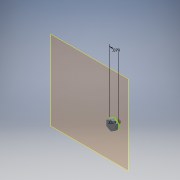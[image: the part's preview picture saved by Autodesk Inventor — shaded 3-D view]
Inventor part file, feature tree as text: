
AUTODESK INVENTOR PART (.ipt)
format: ipt  version: 2016 (Build 200138000, 138)  size: 101,376 bytes
history: native  units: in
note: dims shown in document units (in); Inventor stores cm internally (conversion verified against a paired STEP export)
features: other x3, sketch x1, plane x1
ambient origin geometry x8: Origin, YZ Plane, XZ Plane, XY Plane, X Axis, Y Axis, Z Axis, Center Point
bodies: Solid1 (feature_tree)
feature tree (5):
  other  "nail.ipt"
  other  "Solid1::nail.ipt"
  other  "TaggingFeature1"
  sketch  "Sketch1"  dims[d0=0.3937in]
  plane  "Work Plane1"
